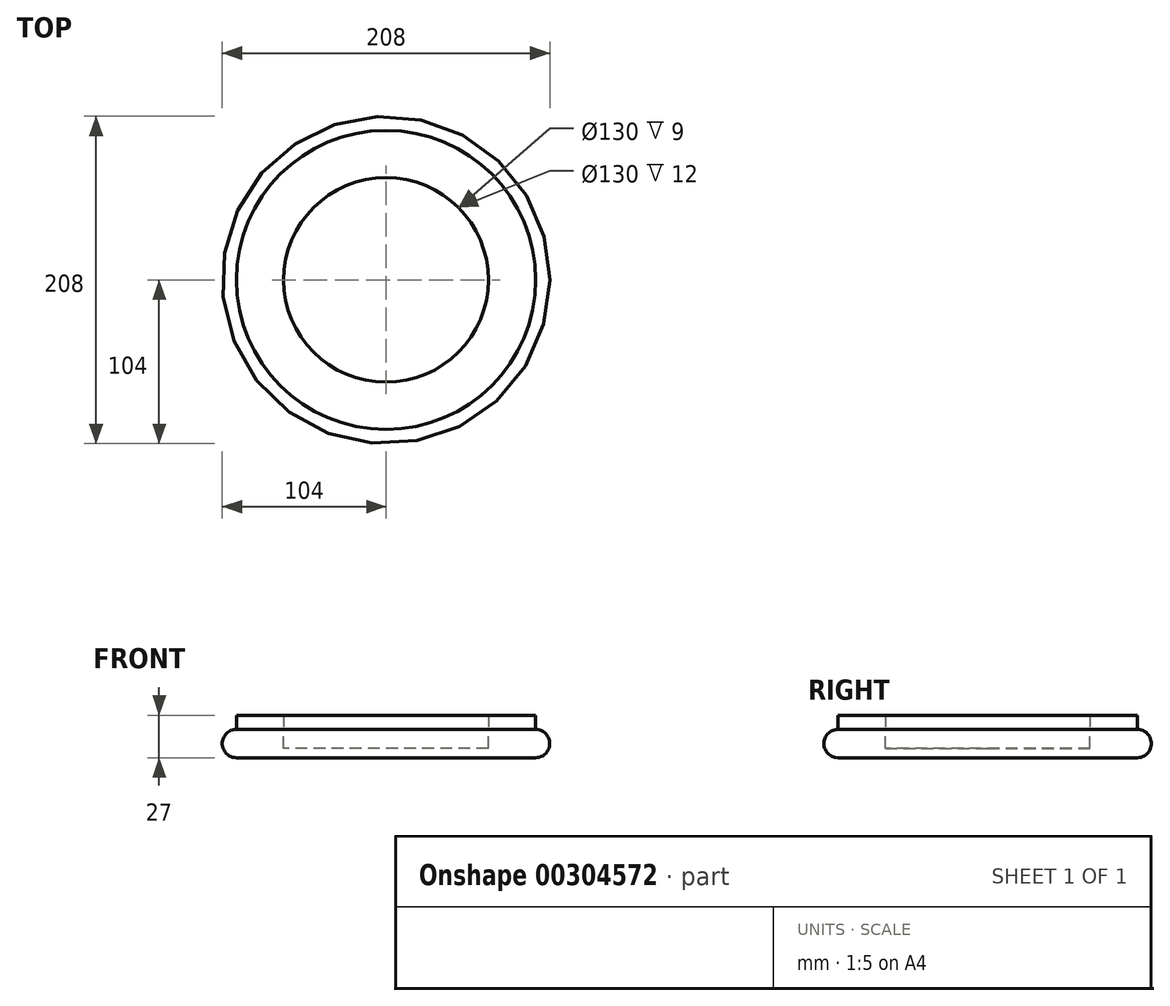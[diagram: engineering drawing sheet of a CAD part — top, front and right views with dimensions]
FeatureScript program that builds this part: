
annotation { "Feature Type Name" : "Feature", "Feature Type Description" : "" }
export const myFeature = defineFeature(function(context is Context, id is Id, definition is map)
    precondition{}
    {
        {
            var Q0;
            Q0=qCreatedBy(makeId("Front.planeOp"),FACE);
            var sketch = newSketch(context, id + "F0", { "sketchPlane" : qUnion([Q0])});
            skLineSegment(sketch, "E0.bottom", {"start": v(0, 0) * mm, "end": v(95, 0) * mm});
            skLineSegment(sketch, "E0.right", {"start": v(95, 0) * mm, "end": v(95, 0) * mm});
            skLineSegment(sketch, "E1.0", {"start": v(0, 6) * mm, "end": v(103.49, 6) * mm});
            skLineSegment(sketch, "E2.0", {"start": v(0, 12) * mm, "end": v(103.49, 12) * mm});
            skLineSegment(sketch, "E3.0", {"start": v(0, 18) * mm, "end": v(95, 18) * mm});
            skLineSegment(sketch, "E4", {"start": v(0, 18) * mm, "end": v(0, 0) * mm});
            skLineSegment(sketch, "E5", {"start": v(95, 18) * mm, "end": v(95, 0) * mm, "construction": true});
            skCircle(sketch, "E6", {"center": v(95, 9) * mm, "radius": 9 * mm});
            skLineSegment(sketch, "E7", {"start": v(65, 18) * mm, "end": v(65, 6) * mm});
            skSolve(sketch);
        }
        {
            var Q0;
            {var subQ0=sQuery(id+"F0.wireOp",EDGE,"E6");var subQ1=sQuery(id+"F0.wireOp",EDGE,"E2.0");var subQ2=makeQuery(id+"F0.imprint","INTERSECT",VERTEX,{"disambiguationData":[OD(0.0)],"derivedFrom":[subQ1,subQ0]});Q0=makeQuery(id+"F0.imprint","IMPRINT",FACE,{"disambiguationData":[TD([[makeQuery(id+"F0.imprint","IMPRINT",EDGE,{"disambiguationData":[TD([[subQ2,1.0]])],"derivedFrom":subQ1}),1.0]])]});}
            var Q1;
            {var subQ0=sQuery(id+"F0.wireOp",EDGE,"E7");var subQ1=sQuery(id+"F0.wireOp",EDGE,"E2.0");var subQ2=makeQuery(id+"F0.imprint","INTERSECT",VERTEX,{"derivedFrom":[subQ1,subQ0]});Q1=makeQuery(id+"F0.imprint","IMPRINT",FACE,{"disambiguationData":[TD([[makeQuery(id+"F0.imprint","IMPRINT",EDGE,{"disambiguationData":[TD([[subQ2,-1.0]])],"derivedFrom":subQ1}),1.0]])]});}
            var Q2;
            {var subQ0=sQuery(id+"F0.wireOp",EDGE,"E7");var subQ1=sQuery(id+"F0.wireOp",EDGE,"E1.0");var subQ2=makeQuery(id+"F0.imprint","INTERSECT",VERTEX,{"derivedFrom":[subQ1,subQ0]});Q2=makeQuery(id+"F0.imprint","IMPRINT",FACE,{"disambiguationData":[TD([[makeQuery(id+"F0.imprint","IMPRINT",EDGE,{"disambiguationData":[TD([[subQ2,-1.0]])],"derivedFrom":subQ1}),1.0]])]});}
            var Q3;
            {var subQ0=sQuery(id+"F0.wireOp",EDGE,"E6");var subQ1=sQuery(id+"F0.wireOp",EDGE,"E1.0");var subQ2=makeQuery(id+"F0.imprint","INTERSECT",VERTEX,{"disambiguationData":[OD(0.0)],"derivedFrom":[subQ1,subQ0]});Q3=makeQuery(id+"F0.imprint","IMPRINT",FACE,{"disambiguationData":[TD([[makeQuery(id+"F0.imprint","IMPRINT",EDGE,{"disambiguationData":[TD([[subQ2,1.0]])],"derivedFrom":subQ1}),1.0]])]});}
            var Q4;
            {var subQ0=sQuery(id+"F0.wireOp",EDGE,"E6");var subQ1=sQuery(id+"F0.wireOp",EDGE,"E1.0");var subQ2=makeQuery(id+"F0.imprint","INTERSECT",VERTEX,{"disambiguationData":[OD(0.0)],"derivedFrom":[subQ1,subQ0]});Q4=makeQuery(id+"F0.imprint","IMPRINT",FACE,{"disambiguationData":[TD([[makeQuery(id+"F0.imprint","IMPRINT",EDGE,{"disambiguationData":[TD([[subQ2,1.0]])],"derivedFrom":subQ1}),-1.0]])]});}
            var Q5;
            {var subQ5=sQuery(id+"F0.wireOp",EDGE,"E0.bottom");Q5=makeQuery(id+"F0.imprint","IMPRINT",FACE,{"disambiguationData":[TD([[makeQuery(id+"F0.imprint","IMPRINT",EDGE,{"derivedFrom":subQ5}),1.0]])]});}
            var Q6;
            Q6=sQuery(id+"F0.wireOp",EDGE,"E4");
            revolve(context, id + "F1", {"entities" : qUnion([Q0, Q1, Q2, Q3, Q4, Q5]), "axis" : qUnion([Q6]), "revolveType" : RevolveType.FULL});
        }
        {
            var Q0;
            Q0=makeQuery(id+"F1.opRevolve","SWEPT_FACE",FACE,{"disambiguationData":[OSD([sQuery(id+"F0.wireOp",EDGE,"E3.0")])]});
            extrude(context, id + "F2", {"entities" : qUnion([Q0]), "depth" : 9 * mm});
        }
    });
